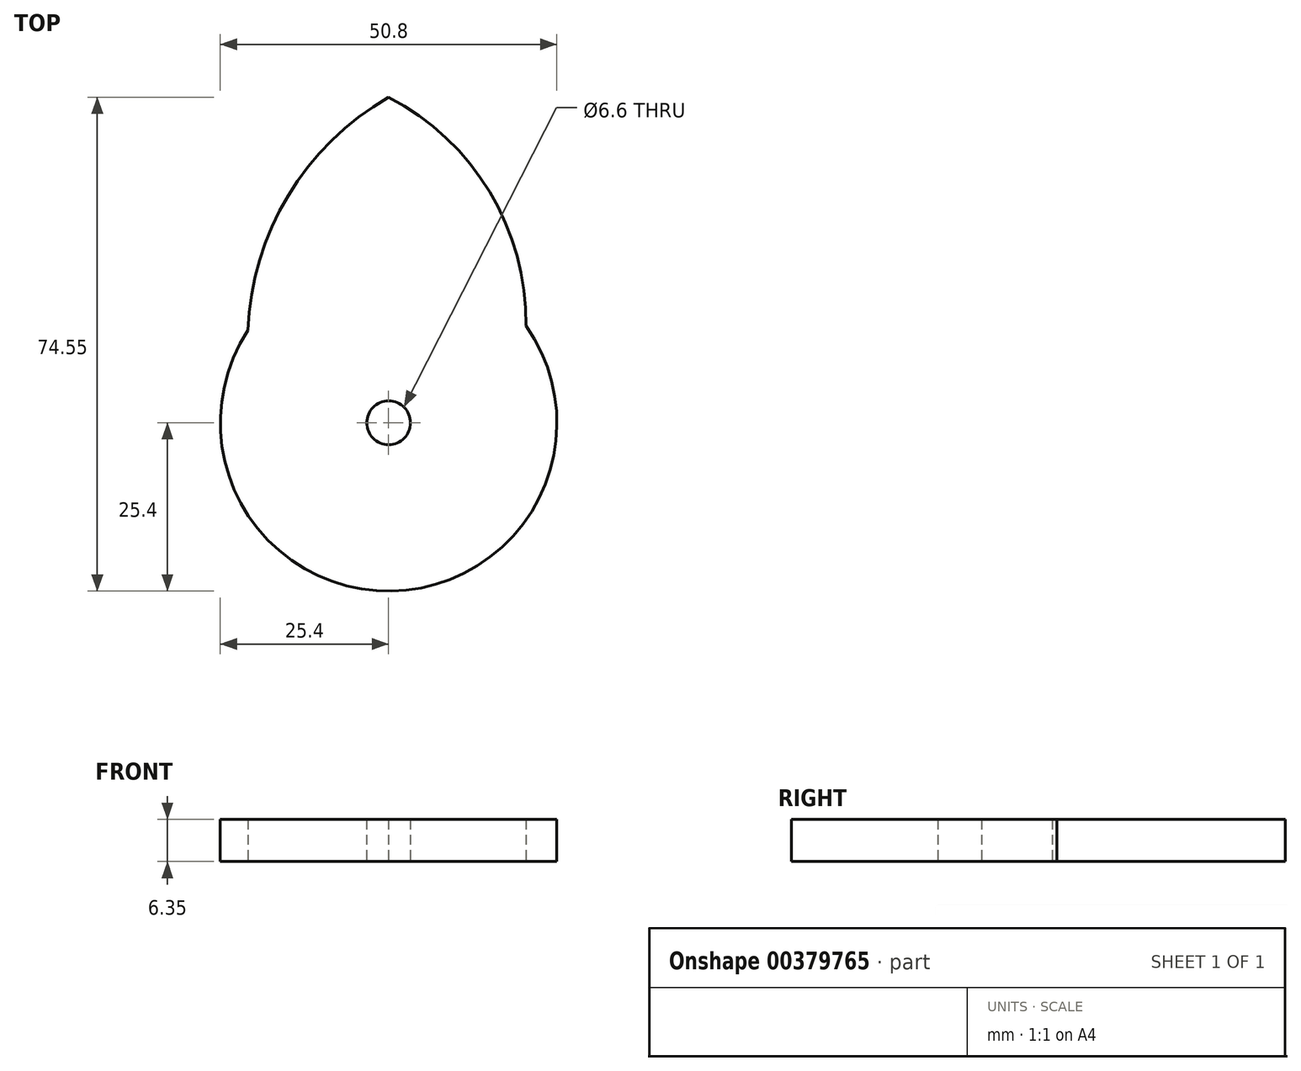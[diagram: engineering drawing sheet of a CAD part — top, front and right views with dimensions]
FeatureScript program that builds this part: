
annotation { "Feature Type Name" : "Feature", "Feature Type Description" : "" }
export const myFeature = defineFeature(function(context is Context, id is Id, definition is map)
    precondition{}
    {
        {
            var Q0;
            Q0=qCreatedBy(makeId("Top.planeOp"),FACE);
            var sketch = newSketch(context, id + "F0", { "sketchPlane" : qUnion([Q0])});
            skCircle(sketch, "E0", {"center": v(0, 0) * mm, "radius": 25.4 * mm});
            skCircle(sketch, "E1", {"center": v(0, 0) * mm, "radius": 3.3 * mm});
            skArc(sketch, "E2", {"start": v(0, 49.15) * mm, "mid": v(-15.17, 34.3) * mm, "end": v(-21.22, 13.97) * mm});
            skArc(sketch, "E3", {"start": v(20.74, 14.66) * mm, "mid": v(15.27, 34.85) * mm, "end": v(0, 49.15) * mm});
            skSolve(sketch);
        }
        {
            var Q0;
            Q0 = qSketchRegion(id + "F0", true);
            extrude(context, id + "F1", {"entities" : qUnion([Q0]), "depth" : 6.35 * mm});
        }
    });
